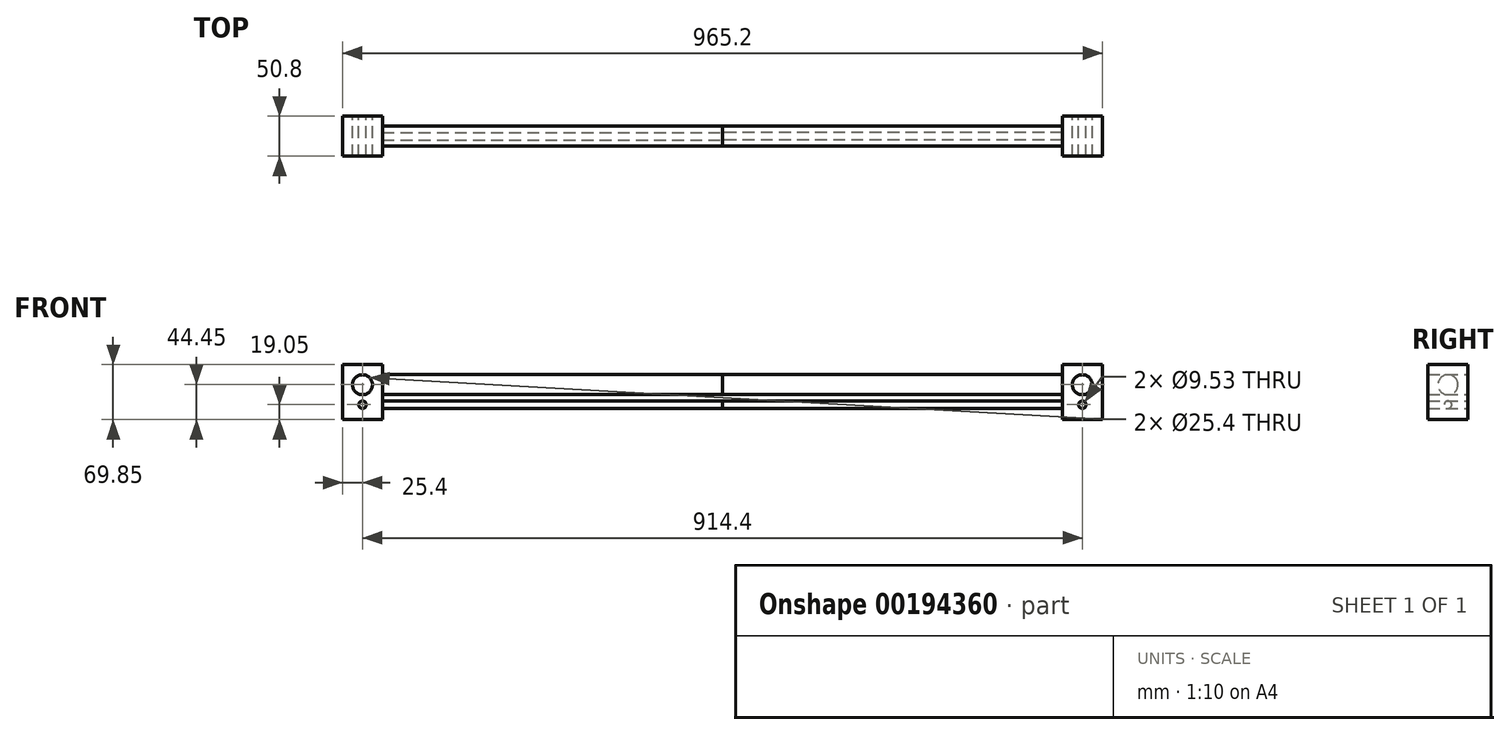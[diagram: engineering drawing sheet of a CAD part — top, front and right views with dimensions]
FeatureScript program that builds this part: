
annotation { "Feature Type Name" : "Feature", "Feature Type Description" : "" }
export const myFeature = defineFeature(function(context is Context, id is Id, definition is map)
    precondition{}
    {
        {
            var Q0;
            Q0=qCreatedBy(makeId("Front.planeOp"),FACE);
            var sketch = newSketch(context, id + "F0", { "sketchPlane" : qUnion([Q0])});
            skCircle(sketch, "E0", {"center": v(-457.2, 0) * mm, "radius": 12.7 * mm});
            skCircle(sketch, "E1", {"center": v(-457.2, -25.4) * mm, "radius": 4.76 * mm});
            skLineSegment(sketch, "E2", {"start": v(-457.2, 0) * mm, "end": v(0, 0) * mm});
            skLineSegment(sketch, "E3", {"start": v(-457.2, 0) * mm, "end": v(-457.2, 12.7) * mm});
            skLineSegment(sketch, "E4", {"start": v(-457.2, 12.7) * mm, "end": v(0, 12.7) * mm});
            skLineSegment(sketch, "E5", {"start": v(0, 12.7) * mm, "end": v(0, 0) * mm});
            skLineSegment(sketch, "E6", {"start": v(-457.2, -25.4) * mm, "end": v(-457.2, -20.64) * mm});
            skLineSegment(sketch, "E7", {"start": v(-457.2, -20.64) * mm, "end": v(0, -20.64) * mm});
            skLineSegment(sketch, "E8", {"start": v(0, -20.64) * mm, "end": v(0, -25.4) * mm});
            skLineSegment(sketch, "E9", {"start": v(0, -25.4) * mm, "end": v(-457.2, -25.4) * mm});
            skLineSegment(sketch, "E10.bottom", {"start": v(-482.6, -44.45) * mm, "end": v(-431.8, -44.45) * mm});
            skLineSegment(sketch, "E10.top", {"start": v(-482.6, 25.4) * mm, "end": v(-431.8, 25.4) * mm});
            skLineSegment(sketch, "E10.left", {"start": v(-482.6, -44.45) * mm, "end": v(-482.6, 25.4) * mm});
            skLineSegment(sketch, "E10.right", {"start": v(-431.8, -44.45) * mm, "end": v(-431.8, 25.4) * mm});
            skSolve(sketch);
        }
        {
            var Q0;
            {var subQ0=sQuery(id+"F0.wireOp",EDGE,"E5");Q0=makeQuery(id+"F0.imprint","IMPRINT",FACE,{"disambiguationData":[TD([[makeQuery(id+"F0.imprint","IMPRINT",EDGE,{"derivedFrom":subQ0}),-1.0]])]});}
            var Q1;
            Q1=sQuery(id+"F0.wireOp",EDGE,"E2");
            revolve(context, id + "F1", {"entities" : qUnion([Q0]), "axis" : qUnion([Q1]), "revolveType" : RevolveType.FULL});
        }
        {
            var Q0;
            {var subQ0=sQuery(id+"F0.wireOp",EDGE,"E8");Q0=makeQuery(id+"F0.imprint","IMPRINT",FACE,{"disambiguationData":[TD([[makeQuery(id+"F0.imprint","IMPRINT",EDGE,{"derivedFrom":subQ0}),-1.0]])]});}
            var Q1;
            Q1=sQuery(id+"F0.wireOp",EDGE,"E9");
            revolve(context, id + "F2", {"entities" : qUnion([Q0]), "axis" : qUnion([Q1]), "revolveType" : RevolveType.FULL});
        }
        {
            var Q0;
            {var subQ8=sQuery(id+"F0.wireOp",EDGE,"E10.bottom");Q0=makeQuery(id+"F0.imprint","IMPRINT",FACE,{"disambiguationData":[TD([[makeQuery(id+"F0.imprint","IMPRINT",EDGE,{"derivedFrom":subQ8}),1.0]])]});}
            var Q1;
            {var subQ3=sQuery(id+"F0.wireOp",EDGE,"E2");var subQ5=sQuery(id+"F0.wireOp",EDGE,"E10.right");var subQ6=makeQuery(id+"F0.imprint","INTERSECT",VERTEX,{"derivedFrom":[subQ3,subQ5]});Q1=makeQuery(id+"F0.imprint","IMPRINT",FACE,{"disambiguationData":[TD([[makeQuery(id+"F0.imprint","IMPRINT",EDGE,{"disambiguationData":[TD([[subQ6,1.0]])],"derivedFrom":subQ3}),1.0]])]});}
            var Q2;
            {var subQ3=sQuery(id+"F0.wireOp",EDGE,"E9");var subQ5=sQuery(id+"F0.wireOp",EDGE,"E10.right");var subQ6=makeQuery(id+"F0.imprint","INTERSECT",VERTEX,{"derivedFrom":[subQ3,subQ5]});Q2=makeQuery(id+"F0.imprint","IMPRINT",FACE,{"disambiguationData":[TD([[makeQuery(id+"F0.imprint","IMPRINT",EDGE,{"disambiguationData":[TD([[subQ6,-1.0]])],"derivedFrom":subQ3}),-1.0]])]});}
            extrude(context, id + "F3", {"entities" : qUnion([Q0, Q1, Q2]), "endBound" : BoundingType.SYMMETRIC, "depth" : 50.8 * mm});
        }
        {
            var Q0;
            Q0=makeQuery(id+"F3.opExtrude","SWEPT_BODY",BODY,{"disambiguationData":[OSD([sQuery(id+"F0.wireOp",EDGE,"E0"),sQuery(id+"F0.wireOp",EDGE,"E1"),sQuery(id+"F0.wireOp",EDGE,"E10.bottom"),sQuery(id+"F0.wireOp",EDGE,"E10.top"),sQuery(id+"F0.wireOp",EDGE,"E10.left"),sQuery(id+"F0.wireOp",EDGE,"E10.right")])]});
            var Q1;
            Q1=makeQuery(id+"F1.opRevolve","SWEPT_BODY",BODY,{"disambiguationData":[OSD([sQuery(id+"F0.wireOp",EDGE,"E2"),sQuery(id+"F0.wireOp",EDGE,"E4"),sQuery(id+"F0.wireOp",EDGE,"E5"),sQuery(id+"F0.wireOp",EDGE,"E10.right")])]});
            var Q2;
            Q2=makeQuery(id+"F2.opRevolve","SWEPT_BODY",BODY,{"disambiguationData":[OSD([sQuery(id+"F0.wireOp",EDGE,"E7"),sQuery(id+"F0.wireOp",EDGE,"E8"),sQuery(id+"F0.wireOp",EDGE,"E9"),sQuery(id+"F0.wireOp",EDGE,"E10.right")])]});
            var Q3;
            Q3=qCreatedBy(makeId("Right.planeOp"),FACE);
            mirror(context, id + "F4", {"entities" : qUnion([Q0, Q1, Q2]), "mirrorPlane" : qUnion([Q3])});
        }
    });
